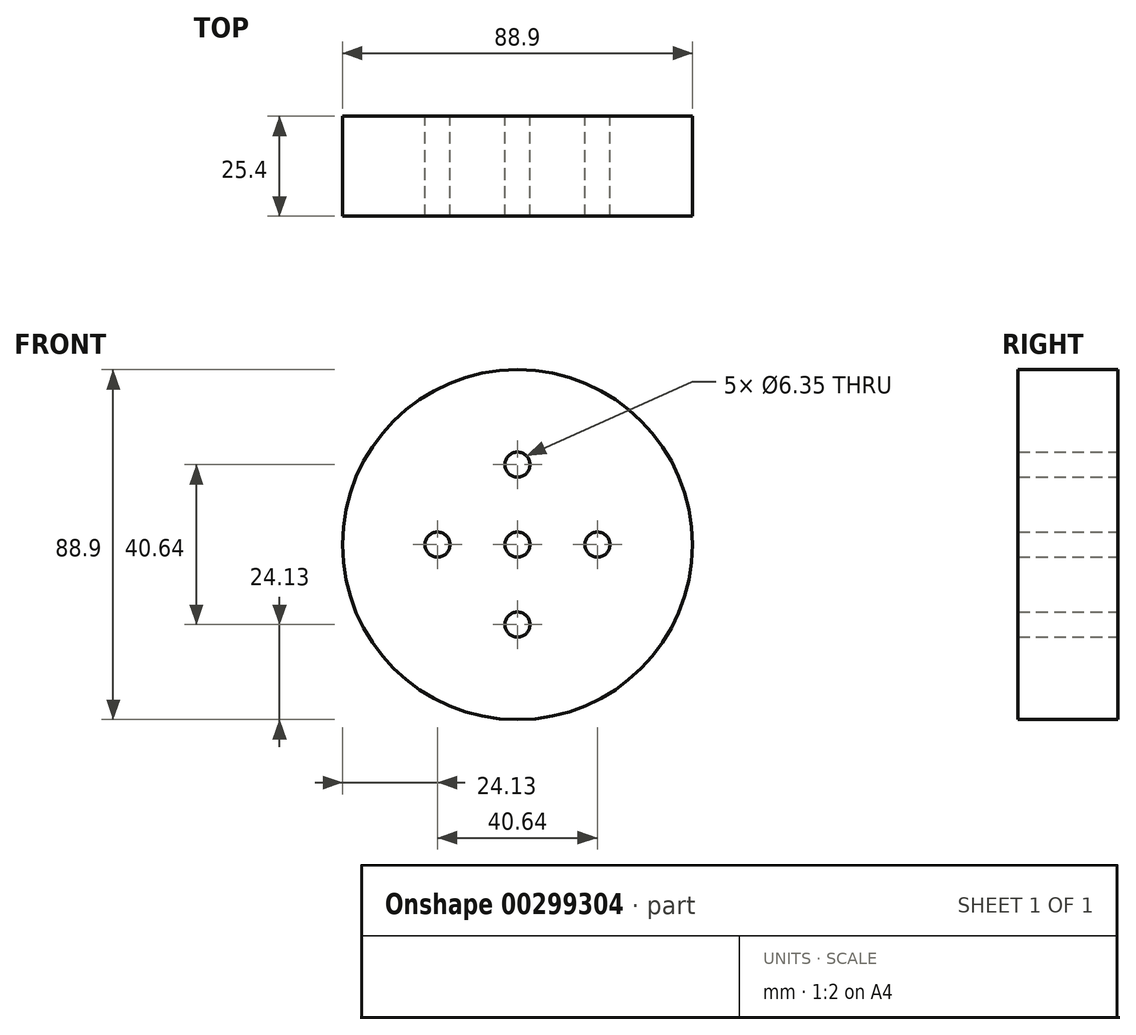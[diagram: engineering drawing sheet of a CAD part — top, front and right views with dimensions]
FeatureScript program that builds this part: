
annotation { "Feature Type Name" : "Feature", "Feature Type Description" : "" }
export const myFeature = defineFeature(function(context is Context, id is Id, definition is map)
    precondition{}
    {
        {
            var Q0;
            Q0=qCreatedBy(makeId("Front.planeOp"),FACE);
            var sketch = newSketch(context, id + "F0", { "sketchPlane" : qUnion([Q0])});
            skCircle(sketch, "E0", {"center": v(0, 0) * mm, "radius": 44.45 * mm});
            skCircle(sketch, "E1", {"center": v(0, 0) * mm, "radius": 3.18 * mm});
            skCircle(sketch, "E2", {"center": v(20.32, 0) * mm, "radius": 3.18 * mm});
            skCircle(sketch, "E3", {"center": v(-20.32, 0) * mm, "radius": 3.18 * mm});
            skCircle(sketch, "E4", {"center": v(0, 20.32) * mm, "radius": 3.18 * mm});
            skCircle(sketch, "E5", {"center": v(0, -20.32) * mm, "radius": 3.18 * mm});
            skSolve(sketch);
        }
        {
            var Q0;
            Q0=makeQuery(id+"F0.imprint","IMPRINT",FACE,{"disambiguationData":[TD([[makeQuery(id+"F0.imprint","IMPRINT",EDGE,{"derivedFrom":sQuery(id+"F0.wireOp",EDGE,"E0")}),1.0]])]});
            extrude(context, id + "F1", {"entities" : qUnion([Q0]), "depth" : 25.4 * mm});
        }
    });
